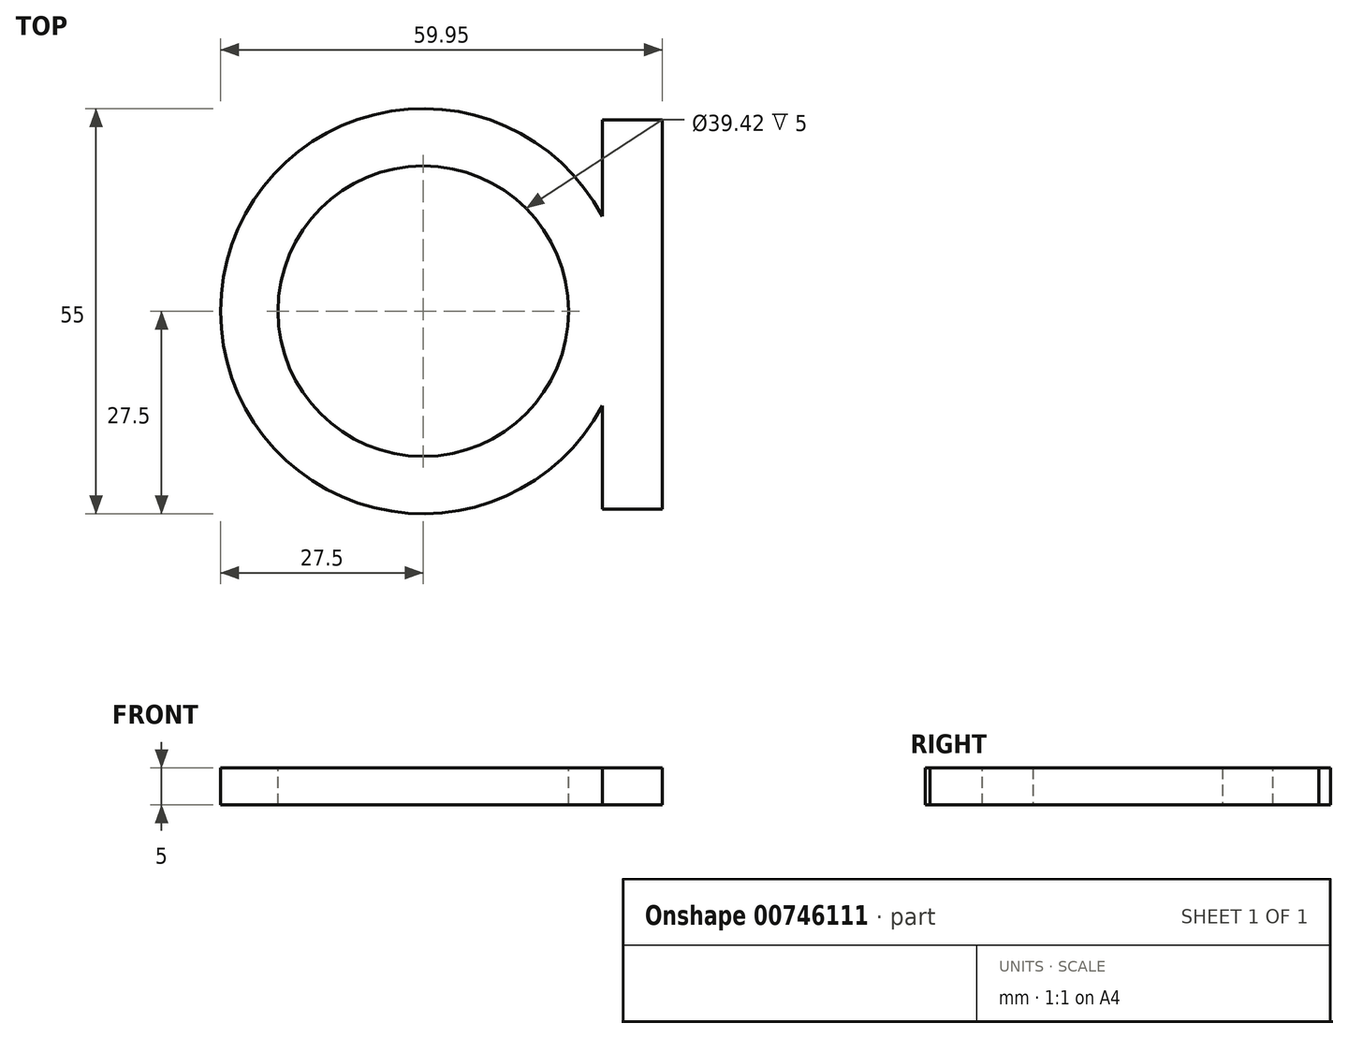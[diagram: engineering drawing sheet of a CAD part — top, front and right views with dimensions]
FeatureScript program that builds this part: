
annotation { "Feature Type Name" : "Feature", "Feature Type Description" : "" }
export const myFeature = defineFeature(function(context is Context, id is Id, definition is map)
    precondition{}
    {
        {
            var Q0;
            Q0=qCreatedBy(makeId("Top.planeOp"),FACE);
            var sketch = newSketch(context, id + "F0", { "sketchPlane" : qUnion([Q0])});
            skCircle(sketch, "E0", {"center": v(0, 0) * mm, "radius": 27.5 * mm});
            skSolve(sketch);
        }
        {
            var Q0;
            Q0=makeQuery(id+"F0.imprint","IMPRINT",FACE,{"disambiguationData":[TD([[makeQuery(id+"F0.imprint","IMPRINT",EDGE,{"derivedFrom":sQuery(id+"F0.wireOp",EDGE,"E0")}),1.0]])]});
            extrude(context, id + "F1", {"entities" : qUnion([Q0]), "depth" : 5 * mm, "offsetDistance" : 25.4 * mm});
        }
        {
            var Q0;
            Q0=makeQuery(id+"F1.opExtrude","CAP_FACE",FACE,{"disambiguationData":[OSD([sQuery(id+"F0.wireOp",EDGE,"E0")])],"isStart":false});
            var sketch = newSketch(context, id + "F2", { "sketchPlane" : qUnion([Q0])});
            skCircle(sketch, "E1", {"center": v(0, 0) * mm, "radius": 19.71 * mm});
            skSolve(sketch);
        }
        {
            var Q0;
            Q0=makeQuery(id+"F2.imprint","IMPRINT",FACE,{"disambiguationData":[TD([[makeQuery(id+"F2.imprint","IMPRINT",EDGE,{"derivedFrom":sQuery(id+"F2.wireOp",EDGE,"E1")}),1.0]])]});
            extrude(context, id + "F3", {"entities" : qUnion([Q0]), "operationType" : NewBodyOperationType.REMOVE, "oppositeDirection" : true, "depth" : 5 * mm, "offsetDistance" : 25.4 * mm});
        }
        {
            var Q0;
            Q0=qCreatedBy(makeId("Top.planeOp"),FACE);
            var sketch = newSketch(context, id + "F4", { "sketchPlane" : qUnion([Q0])});
            skLineSegment(sketch, "E2.bottom", {"start": v(24.3, 25.93) * mm, "end": v(32.45, 25.93) * mm});
            skLineSegment(sketch, "E2.top", {"start": v(24.3, -26.86) * mm, "end": v(32.45, -26.86) * mm});
            skLineSegment(sketch, "E2.left", {"start": v(24.3, 25.93) * mm, "end": v(24.3, -26.86) * mm});
            skLineSegment(sketch, "E2.right", {"start": v(32.45, 25.93) * mm, "end": v(32.45, -26.86) * mm});
            skSolve(sketch);
        }
        {
            var Q0;
            Q0=makeQuery(id+"F4.imprint","IMPRINT",FACE,{"disambiguationData":[TD([[makeQuery(id+"F4.imprint","IMPRINT",EDGE,{"derivedFrom":sQuery(id+"F4.wireOp",EDGE,"E2.bottom")}),-1.0]])]});
            extrude(context, id + "F5", {"entities" : qUnion([Q0]), "operationType" : NewBodyOperationType.ADD, "depth" : 5 * mm, "offsetDistance" : 25.4 * mm});
        }
    });
